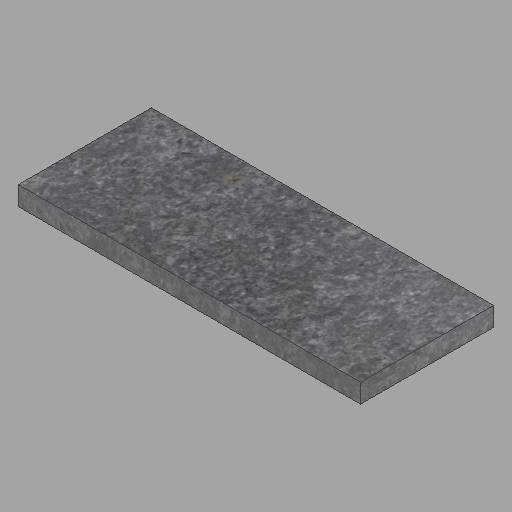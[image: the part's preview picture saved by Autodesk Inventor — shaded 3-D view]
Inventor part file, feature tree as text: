
AUTODESK INVENTOR PART (.ipt)
format: ipt  version: 2023 (Build 270158000, 158)  size: 222,208 bytes
history: native  units: in
note: dims shown in document units (in); Inventor stores cm internally (conversion verified against a paired STEP export)
features: other x1, extrude x1, sketch x1
ambient origin geometry x8: Origin, YZ Plane, XZ Plane, XY Plane, X Axis, Y Axis, Z Axis, Center Point
bodies: Solid1 (feature_tree)
feature tree (3):
  other  "2x14x36-15"
  extrude  "Extrusion1"  Depth=2.0in
  sketch  "Sketch1"  dims[d0=14.0in d1=2.0in d2=36.0in d3=0.0in]
